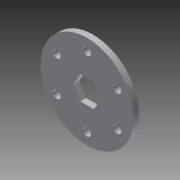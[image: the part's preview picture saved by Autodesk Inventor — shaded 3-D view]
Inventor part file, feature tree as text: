
AUTODESK INVENTOR PART (.ipt)
format: ipt  version: 2014 (Build 180170000, 170)  size: 101,376 bytes
history: native  units: in
note: dims shown in document units (in); Inventor stores cm internally (conversion verified against a paired STEP export)
features: extrude x1, sketch x1
ambient origin geometry x8: Origin, YZ Plane, XZ Plane, XY Plane, X Axis, Y Axis, Z Axis, Center Point
bodies: Solid1 (feature_tree)
feature tree (2):
  extrude  "Extrusion1"  Depth=0.504in
  sketch  "Sketch1"  dims[d0=2.0in d1=0.504in d2=0.164in d3=0.75in d4=2.3622in d6=360.0deg d8=0.125in d9=0.0in]
